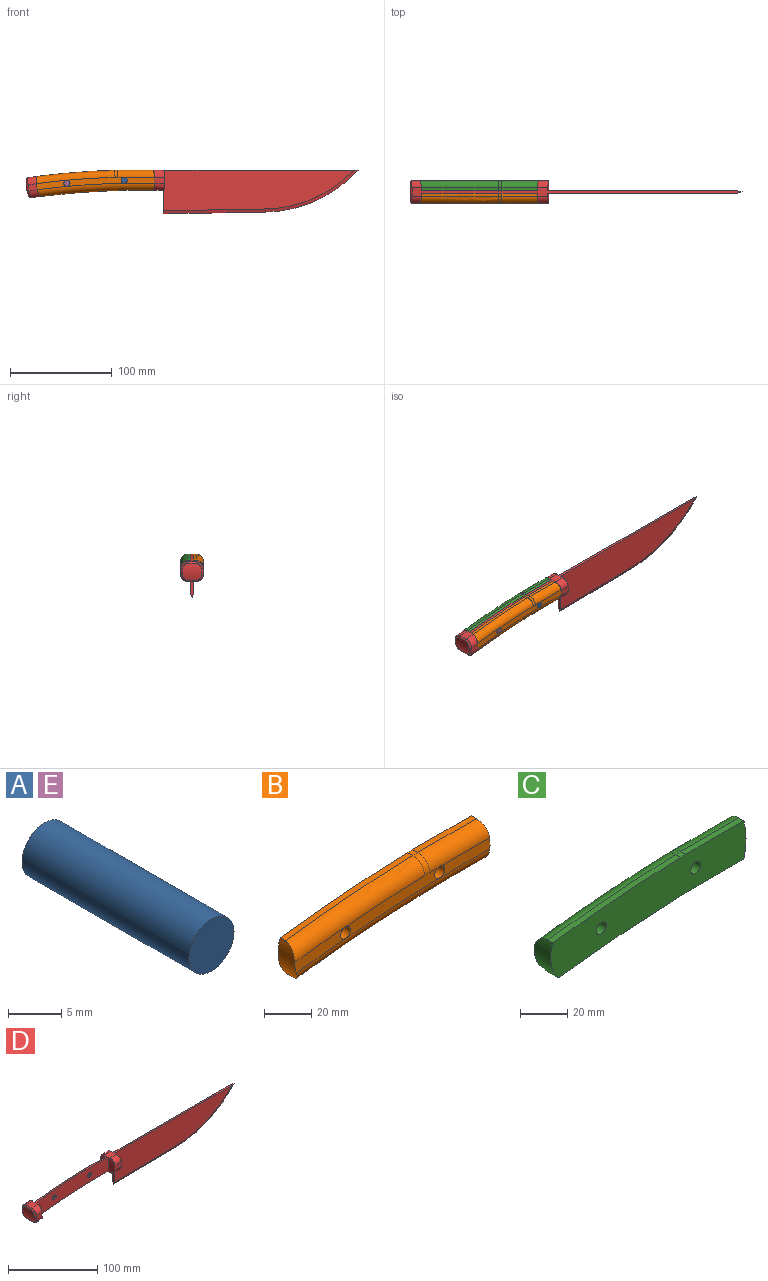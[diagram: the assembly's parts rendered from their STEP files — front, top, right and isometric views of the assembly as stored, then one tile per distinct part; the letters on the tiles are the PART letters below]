
ASSEMBLY  parts=5 mates=10
PART A: 3 faces, bbox 6x22.2x6 mm
  f0: cylinder r=3mm len=22.2mm, axis (0,1,0), area 418.5mm2, adj f1,f2
  f1: plane 6x6mm, normal (0,-1,0), area 28.3mm2, adj f0
  f2: plane 6x6mm, normal (0,1,0), area 28.3mm2, adj f0
PART B: 16 faces, bbox 117.6x10x27.1 mm
  f0: plane 30.53x9.25mm, normal (0,-1,0), area 166.5mm2, adj f3,f8,f12,f15
  f1: plane 56.58x8.93mm, normal (0,-1,0), area 309.2mm2, adj f7,f8,f12,f13,f14,f15
  f2: cylinder r=800mm len=76.12mm, axis (0,1,0), area 229.2mm2, adj f3,f9,f11,f12
  f3: cylinder r=20.5mm len=19.74mm, axis (0,1,0), area 185.9mm2, adj f0,f2,f4,f11,f12,f15
  f4: cylinder r=780mm len=110.81mm, axis (0,1,0), area 333.2mm2, adj f3,f5,f11,f15
  f5: cylinder r=40mm len=19.77mm, axis (0,1,0), area 178.3mm2, adj f4,f6,f10,f11,f14,f15
  f6: plane 34.8x3mm, normal (0,0,1), area 104.4mm2, adj f5,f9,f11,f14
  f7: cylinder r=3mm len=10mm, axis (0,1,0), area 188.5mm2, adj f1,f10,f11,f14
  f8: cylinder r=3mm len=10mm, axis (0,1,0), area 188.5mm2, adj f0,f1,f11
  f9: cylinder r=100mm len=3.11mm, axis (0,1,0), area 9.3mm2, adj f2,f6,f11,f13
  f10: plane 29.94x5.82mm, normal (0,-1,0), area 157.1mm2, adj f5,f7,f14,f15
  f11: plane 116.51x25.81mm, normal (0,1,0), area 2239.6mm2, adj f2,f3,f4,f5,f6,f7,f8,f9
  f12: torus R=793mm, axis (0,-1,0), area 847.7mm2, adj f0,f1,f2,f3,f13
  f13: torus R=93mm, axis (0,-1,0), area 33.3mm2, adj f1,f9,f12,f14
  f14: cylinder r=7mm len=35.96mm, axis (1,0,0), area 388mm2, adj f1,f5,f6,f7,f10,f13
  f15: torus R=787mm, axis (0,-1,0), area 1243.1mm2, adj f0,f1,f3,f4,f5,f10
PART C: 16 faces, bbox 117.6x12x27.1 mm
  f0: plane 29.94x5.82mm, normal (0,1,0), area 157.1mm2, adj f5,f7,f14,f15
  f1: plane 56.58x8.93mm, normal (0,1,0), area 309.2mm2, adj f7,f8,f12,f13,f14,f15
  f2: cylinder r=800mm len=76.12mm, axis (0,1,0), area 229.2mm2, adj f3,f9,f10,f12
  f3: cylinder r=20.5mm len=19.74mm, axis (0,1,0), area 185.9mm2, adj f2,f4,f10,f11,f12,f15
  f4: cylinder r=780mm len=110.81mm, axis (0,1,0), area 333.2mm2, adj f3,f5,f10,f15
  f5: cylinder r=40mm len=19.77mm, axis (0,1,0), area 178.3mm2, adj f0,f4,f6,f10,f14,f15
  f6: plane 34.8x3mm, normal (0,0,1), area 104.4mm2, adj f5,f9,f10,f14
  f7: cylinder r=3mm len=10mm, axis (0,1,0), area 188.5mm2, adj f0,f1,f10,f14
  f8: cylinder r=3mm len=10mm, axis (0,1,0), area 188.5mm2, adj f1,f10,f11
  f9: cylinder r=100mm len=3.11mm, axis (0,1,0), area 9.3mm2, adj f2,f6,f10,f13
  f10: plane 116.51x25.81mm, normal (0,-1,0), area 2239.6mm2, adj f2,f3,f4,f5,f6,f7,f8,f9
  f11: plane 30.53x9.25mm, normal (0,1,0), area 166.5mm2, adj f3,f8,f12,f15
  f12: torus R=793mm, axis (0,-1,0), area 847.7mm2, adj f1,f2,f3,f11,f13
  f13: torus R=93mm, axis (0,-1,0), area 33.3mm2, adj f1,f9,f12,f14
  f14: cylinder r=7mm len=35.96mm, axis (-1,0,0), area 388mm2, adj f0,f1,f5,f6,f7,f13
  f15: torus R=787mm, axis (0,-1,0), area 1243.1mm2, adj f0,f1,f3,f4,f5,f11
PART D: 42 faces, bbox 326.6x22.3x45 mm
  f0: plane 116.51x25.81mm, normal (0,1,0), area 2239.6mm2, adj f2,f3,f5,f14,f17,f27,f40,f41
  f1: plane 116.51x25.81mm, normal (0,-1,0), area 2239.6mm2, adj f2,f3,f5,f9,f12,f27,f40,f41
  f2: plane 235.99x8.24mm, normal (0,0,1), area 576.1mm2, adj f0,f1,f7,f8,f9,f10,f14,f15
  f3: cylinder r=800mm len=85.36mm, axis (0,1,0), area 244.5mm2, adj f0,f1,f12,f17,f19,f23,f27,f37
  f4: cylinder r=30.5mm len=18.2mm, axis (0,1,0), area 292.2mm2, adj f32,f33,f34,f35,f36,f37,f38,f39
  f5: cylinder r=780mm len=130.53mm, axis (0,1,0), area 406.8mm2, adj f0,f1,f6,f9,f10,f12,f14,f15
  f6: plane 22.91x2.2mm, normal (-1,0,0), area 47.1mm2, adj f5,f7,f8,f28,f29
  f7: plane 186.77x39.9mm, normal (0,-1,0), area 6150.7mm2, adj f2,f6,f10,f28,f30
  f8: plane 186.77x39.9mm, normal (0,1,0), area 6150.7mm2, adj f2,f6,f15,f29,f31
  f9: cylinder r=40mm len=19.77mm, axis (0,1,0), area 178.3mm2, adj f1,f2,f5,f11,f25,f26
  f10: cylinder r=50mm len=20.01mm, axis (0,1,0), area 180.2mm2, adj f2,f5,f7,f11,f25,f26
  f11: plane 10.11x6.03mm, normal (0,-1,0), area 59mm2, adj f9,f10,f25,f26
  f12: cylinder r=20.5mm len=19.74mm, axis (0,1,0), area 185.9mm2, adj f1,f3,f5,f13,f23,f24
  f13: plane 8.93x7.01mm, normal (0,-1,0), area 48.1mm2, adj f12,f23,f24,f33
  f14: cylinder r=40mm len=19.77mm, axis (0,-1,0), area 178.3mm2, adj f0,f2,f5,f16,f21,f22
  f15: cylinder r=50mm len=20.01mm, axis (0,-1,0), area 180.2mm2, adj f2,f5,f8,f16,f21,f22
  f16: plane 10.11x6.03mm, normal (0,1,0), area 59mm2, adj f14,f15,f21,f22
  f17: cylinder r=20.5mm len=19.74mm, axis (0,-1,0), area 185.9mm2, adj f0,f3,f5,f18,f19,f20
  f18: plane 8.93x7.01mm, normal (0,1,0), area 48.1mm2, adj f17,f19,f20,f38
  f19: torus R=793mm, axis (0,1,0), area 96mm2, adj f3,f17,f18,f39
  f20: torus R=787mm, axis (0,1,0), area 98mm2, adj f5,f17,f18,f36
  f21: torus R=787mm, axis (0,1,0), area 111.2mm2, adj f5,f14,f15,f16
  f22: cylinder r=7mm len=11.18mm, axis (1,0,0), area 111.7mm2, adj f2,f14,f15,f16
  f23: torus R=793mm, axis (0,-1,0), area 96mm2, adj f3,f12,f13,f35
  f24: torus R=787mm, axis (0,-1,0), area 98mm2, adj f5,f12,f13,f32
  f25: torus R=787mm, axis (0,-1,0), area 111.2mm2, adj f5,f9,f10,f11
  f26: cylinder r=7mm len=11.18mm, axis (1,0,0), area 111.7mm2, adj f2,f9,f10,f11
  f27: cylinder r=100mm len=3.11mm, axis (0,1,0), area 6.8mm2, adj f0,f1,f2,f3
  f28: plane 100x4.77mm, normal (0.01,-0.94,-0.34), area 321.6mm2, adj f6,f7,f29,f30
  f29: plane 100x4.77mm, normal (0.01,0.94,-0.34), area 321.6mm2, adj f6,f8,f28,f31
  f30: cone r=122.76mm half-angle=70deg, axis (0,1,0), area 321.5mm2, adj f2,f7,f28,f31
  f31: cone r=125.86mm half-angle=70deg, axis (0,-1,0), area 321.5mm2, adj f2,f8,f29,f30
  f32: bspline ~8.53x8.5mm, area 28.1mm2, adj f4,f24,f33,f34
  f33: torus R=28.5mm, axis (0,-1,0), area 19.7mm2, adj f4,f13,f32,f35
  f34: cylinder r=2mm len=8.2mm, axis (0,-1,0), area 20.8mm2, adj f4,f5,f32,f36
  f35: bspline ~8.77x8.54mm, area 28.5mm2, adj f4,f23,f33,f37
  f36: bspline ~8.5x7.4mm, area 28.1mm2, adj f4,f20,f34,f38
  f37: cylinder r=2mm len=8.2mm, axis (0,1,0), area 21.3mm2, adj f3,f4,f35,f39
  f38: torus R=28.5mm, axis (0,1,0), area 19.7mm2, adj f4,f18,f36,f39
  f39: bspline ~8.77x8.54mm, area 28.5mm2, adj f4,f19,f37,f38
  f40: cylinder r=3mm len=6mm, axis (0,-1,0), area 41.5mm2, adj f0,f1
  f41: cylinder r=3mm len=6mm, axis (0,-1,0), area 41.5mm2, adj f0,f1
PART E: same geometry as A
PLACE A rot(axis=(0,-1,0),90deg) t=(-66.69,11.12,11.64)mm
PLACE B t=(-89.48,-1.08,12.36)mm
PLACE C t=(-89.48,11.12,12.36)mm
PLACE D t=(-27.7,0.02,21.46)mm fixed
PLACE E rot(axis=(0,1,0),90deg) t=(-122.94,11.12,8.52)mm
MATE cylindrical C.f7 <-> A.f0  axis (0,1,0) through (-66.69,6.12,11.64)mm
MATE cylindrical E.f0 <-> C.f8  axis (0,1,0) through (-122.94,0.02,8.52)mm
MATE planar B.f11 <-> D.f1  axis (0,1,0) through (-94.85,-1.08,9.88)mm
MATE cylindrical B.f7 <-> A.f0  axis (0,1,0) through (-66.69,-6.08,11.64)mm
MATE planar E.f0 <-> B.f1  axis (0,-1,0) through (-122.94,-11.08,8.52)mm
MATE cylindrical E.f0 <-> B.f8  axis (0,1,0) through (-122.94,0.02,8.52)mm
MATE cylindrical E.f0 <-> D.f41  axis (0,1,0) through (-122.94,0.02,8.52)mm
MATE planar E.f0 <-> C.f1  axis (0,1,0) through (-122.94,11.12,8.52)mm
MATE cylindrical A.f0 <-> D.f40  axis (0,1,0) through (-66.69,0.02,11.64)mm
MATE planar A.f0 <-> B.f1  axis (0,-1,0) through (-66.69,-11.08,11.64)mm
